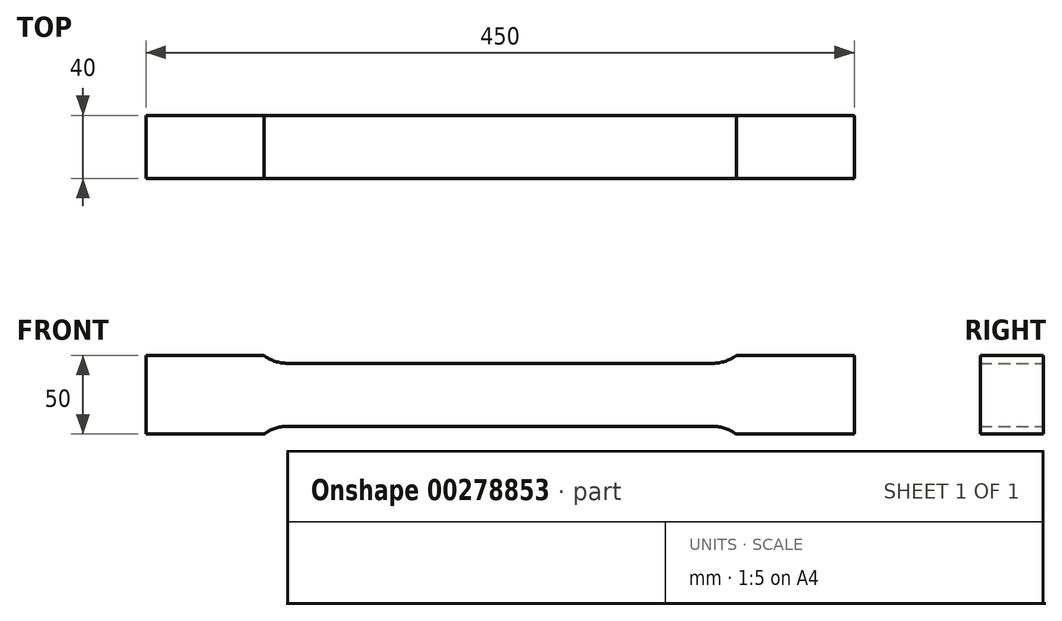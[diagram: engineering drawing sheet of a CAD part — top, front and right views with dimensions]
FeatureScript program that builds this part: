
annotation { "Feature Type Name" : "Feature", "Feature Type Description" : "" }
export const myFeature = defineFeature(function(context is Context, id is Id, definition is map)
    precondition{}
    {
        {
            var Q0;
            Q0=qCreatedBy(makeId("Front.planeOp"),FACE);
            var sketch = newSketch(context, id + "F0", { "sketchPlane" : qUnion([Q0])});
            skLineSegment(sketch, "E0", {"start": v(0, 20) * mm, "end": v(135, 20) * mm});
            skArc(sketch, "E1", {"start": v(135, 20) * mm, "mid": v(142.9, 21.28) * mm, "end": v(150, 25) * mm});
            skLineSegment(sketch, "E2", {"start": v(150, 25) * mm, "end": v(225, 25) * mm});
            skLineSegment(sketch, "E3", {"start": v(225, 25) * mm, "end": v(225, 0) * mm});
            skLineSegment(sketch, "E4.MirrorCS", {"start": v(0, -20) * mm, "end": v(135, -20) * mm});
            skLineSegment(sketch, "E5.MirrorCS", {"start": v(225, -25) * mm, "end": v(225, 0) * mm});
            skLineSegment(sketch, "E6.MirrorCS", {"start": v(150, -25) * mm, "end": v(225, -25) * mm});
            skArc(sketch, "E7.MirrorCS", {"start": v(135, -20) * mm, "mid": v(142.9, -21.28) * mm, "end": v(150, -25) * mm});
            skArc(sketch, "E8.MirrorCS", {"start": v(-135, -20) * mm, "mid": v(-142.9, -21.28) * mm, "end": v(-150, -25) * mm});
            skLineSegment(sketch, "E9.MirrorCS", {"start": v(-150, -25) * mm, "end": v(-225, -25) * mm});
            skLineSegment(sketch, "E10.MirrorCS", {"start": v(0, 20) * mm, "end": v(-135, 20) * mm});
            skArc(sketch, "E11.MirrorCS", {"start": v(-135, 20) * mm, "mid": v(-142.9, 21.28) * mm, "end": v(-150, 25) * mm});
            skLineSegment(sketch, "E12.MirrorCS", {"start": v(-150, 25) * mm, "end": v(-225, 25) * mm});
            skLineSegment(sketch, "E13.MirrorCS", {"start": v(-225, -25) * mm, "end": v(-225, 0) * mm});
            skLineSegment(sketch, "E14.MirrorCS", {"start": v(-225, 25) * mm, "end": v(-225, 0) * mm});
            skLineSegment(sketch, "E15.MirrorCS", {"start": v(0, -20) * mm, "end": v(-135, -20) * mm});
            skSolve(sketch);
        }
        {
            var Q0;
            Q0=makeQuery(id+"F0.imprint","IMPRINT",FACE,{"disambiguationData":[TD([[makeQuery(id+"F0.imprint","IMPRINT",EDGE,{"derivedFrom":sQuery(id+"F0.wireOp",EDGE,"E1")}),-1.0]])]});
            extrude(context, id + "F1", {"entities" : qUnion([Q0]), "endBound" : BoundingType.SYMMETRIC, "depth" : 40 * mm});
        }
    });
